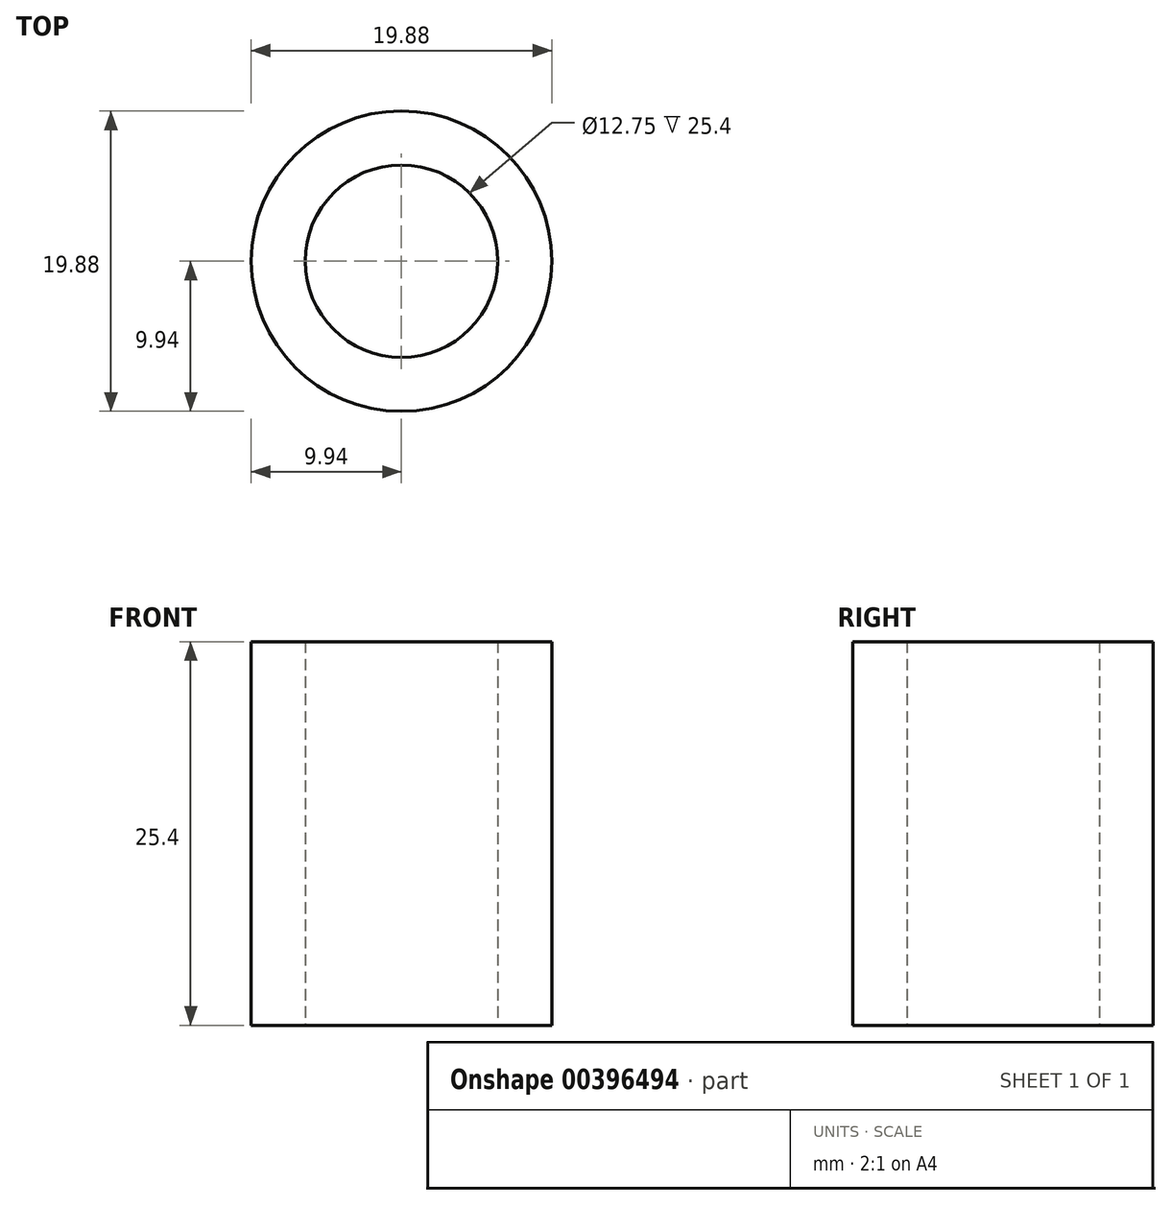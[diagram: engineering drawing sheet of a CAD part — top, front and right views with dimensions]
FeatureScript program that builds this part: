
annotation { "Feature Type Name" : "Feature", "Feature Type Description" : "" }
export const myFeature = defineFeature(function(context is Context, id is Id, definition is map)
    precondition{}
    {
        {
            var Q0;
            Q0=qCreatedBy(makeId("Top.planeOp"),FACE);
            var sketch = newSketch(context, id + "F0", { "sketchPlane" : qUnion([Q0])});
            skCircle(sketch, "E0", {"center": v(0, 0) * mm, "radius": 9.94 * mm});
            skCircle(sketch, "E1", {"center": v(0, 0) * mm, "radius": 6.37 * mm});
            skSolve(sketch);
        }
        {
            var Q0;
            Q0 = qSketchRegion(id + "F0", true);
            extrude(context, id + "F1", {"entities" : qUnion([Q0]), "depth" : 25.4 * mm});
        }
    });
